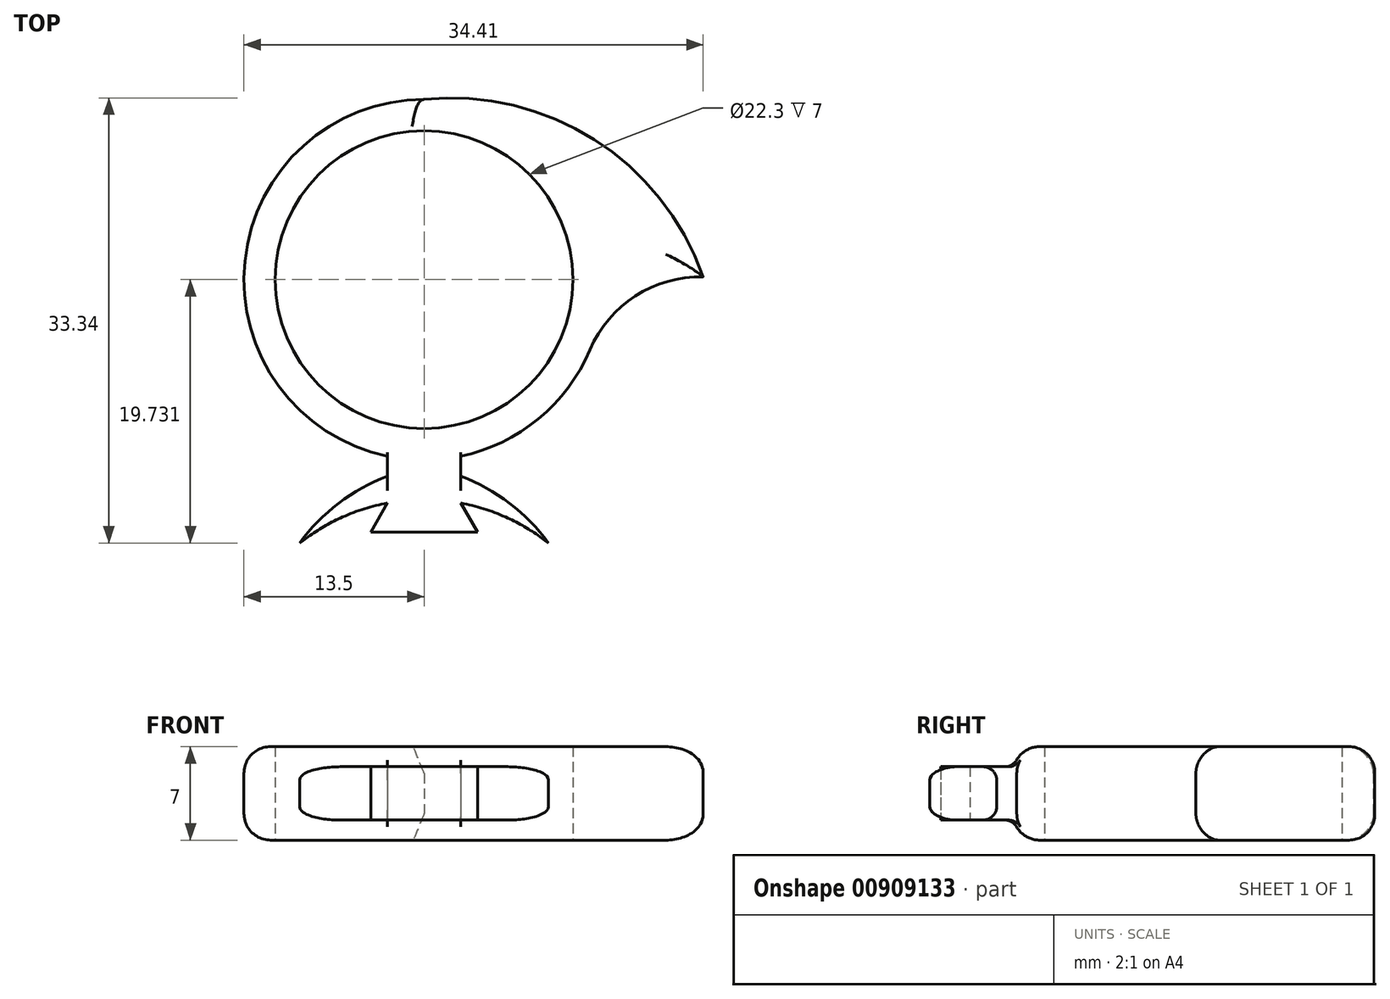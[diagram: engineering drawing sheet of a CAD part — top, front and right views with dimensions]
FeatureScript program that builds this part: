
annotation { "Feature Type Name" : "Feature", "Feature Type Description" : "" }
export const myFeature = defineFeature(function(context is Context, id is Id, definition is map)
    precondition{}
    {
        {
            var Q0;
            Q0=qCreatedBy(makeId("Top.planeOp"),FACE);
            var sketch = newSketch(context, id + "F0", { "sketchPlane" : qUnion([Q0])});
            skLineSegment(sketch, "E0", {"start": v(0, 0) * mm, "end": v(-4, 0) * mm});
            skLineSegment(sketch, "E1", {"start": v(-4, 0) * mm, "end": v(-2.75, 2.17) * mm});
            skLineSegment(sketch, "E2.MirrorCS", {"start": v(4, 0) * mm, "end": v(2.75, 2.17) * mm});
            skLineSegment(sketch, "E3.MirrorCS", {"start": v(0, 0) * mm, "end": v(4, 0) * mm});
            skPoint(sketch, "E4", {"position": v(0, 2.42) * mm});
            skCircle(sketch, "E5", {"center": v(0, 18.9) * mm, "radius": 11.15 * mm});
            skLineSegment(sketch, "E6", {"start": v(-2.75, 4.18) * mm, "end": v(-2.75, 5.68) * mm});
            skLineSegment(sketch, "E7", {"start": v(2.75, 4.18) * mm, "end": v(2.75, 5.68) * mm});
            skArc(sketch, "E8", {"start": v(20.91, 19.1) * mm, "mid": v(15.83, 17.67) * mm, "end": v(12.43, 13.64) * mm});
            skArc(sketch, "E9", {"start": v(20.91, 19.1) * mm, "mid": v(12.76, 29.38) * mm, "end": v(0, 32.4) * mm});
            skPoint(sketch, "E10", {"position": v(-9.32, -0.83) * mm});
            skPoint(sketch, "E11.MirrorP", {"position": v(9.32, -0.83) * mm});
            skArc(sketch, "E12", {"start": v(-2.75, 4.18) * mm, "mid": v(-6.4, 2.16) * mm, "end": v(-9.32, -0.83) * mm});
            skArc(sketch, "E13.MirrorCS", {"start": v(2.75, 4.18) * mm, "mid": v(6.4, 2.16) * mm, "end": v(9.32, -0.83) * mm});
            skArc(sketch, "E14", {"start": v(-2.75, 2.17) * mm, "mid": v(-6.22, 1.07) * mm, "end": v(-9.32, -0.83) * mm});
            skArc(sketch, "E15.MirrorCS", {"start": v(2.75, 2.17) * mm, "mid": v(6.22, 1.07) * mm, "end": v(9.32, -0.83) * mm});
            skArc(sketch, "E16", {"start": v(2.75, 2.17) * mm, "mid": v(0, 2.42) * mm, "end": v(-2.75, 2.17) * mm});
            skCircle(sketch, "E17", {"center": v(0, 18.9) * mm, "radius": 13.5 * mm});
            skSolve(sketch);
        }
        {
            var Q0;
            Q0=makeQuery(id+"F0.imprint","IMPRINT",FACE,{"disambiguationData":[TD([[makeQuery(id+"F0.imprint","IMPRINT",EDGE,{"derivedFrom":sQuery(id+"F0.wireOp",EDGE,"E5")}),-1.0]])]});
            var Q1;
            {var subQ0=sQuery(id+"F0.wireOp",EDGE,"E8");Q1=makeQuery(id+"F0.imprint","IMPRINT",FACE,{"disambiguationData":[TD([[makeQuery(id+"F0.imprint","IMPRINT",EDGE,{"derivedFrom":subQ0}),-1.0]])]});}
            extrude(context, id + "F1", {"entities" : qUnion([Q0, Q1]), "endBound" : BoundingType.SYMMETRIC, "depth" : 7 * mm, "offsetDistance" : 25 * mm});
        }
        {
            var Q0;
            {var subQ1=sQuery(id+"F0.wireOp",EDGE,"E6");Q0=makeQuery(id+"F0.imprint","IMPRINT",FACE,{"disambiguationData":[TD([[makeQuery(id+"F0.imprint","IMPRINT",EDGE,{"derivedFrom":subQ1}),-1.0]])]});}
            var Q1;
            Q1=makeQuery(id+"F0.imprint","IMPRINT",FACE,{"disambiguationData":[TD([[makeQuery(id+"F0.imprint","IMPRINT",EDGE,{"derivedFrom":sQuery(id+"F0.wireOp",EDGE,"E0")}),-1.0]])]});
            extrude(context, id + "F2", {"entities" : qUnion([Q0, Q1]), "operationType" : NewBodyOperationType.ADD, "endBound" : BoundingType.SYMMETRIC, "depth" : 4 * mm, "offsetDistance" : 25 * mm});
        }
        {
            var Q0;
            Q0=makeQuery(id+"F0.imprint","IMPRINT",FACE,{"disambiguationData":[TD([[makeQuery(id+"F0.imprint","IMPRINT",EDGE,{"derivedFrom":sQuery(id+"F0.wireOp",EDGE,"E0")}),-1.0]])]});
            extrude(context, id + "F3", {"entities" : qUnion([Q0]), "operationType" : NewBodyOperationType.ADD, "endBound" : BoundingType.SYMMETRIC, "depth" : 4 * mm, "offsetDistance" : 25 * mm});
        }
        {
            var Q0;
            Q0=makeQuery(id+"F1.opExtrude","CAP_EDGE",EDGE,{"disambiguationData":[OSD([sQuery(id+"F0.wireOp",EDGE,"E9")])],"isStart":true});
            var Q1;
            Q1=makeQuery(id+"F1.opExtrude","CAP_EDGE",EDGE,{"disambiguationData":[OSD([sQuery(id+"F0.wireOp",EDGE,"E9")])],"isStart":false});
            var Q2;
            {var subQ0=sQuery(id+"F0.wireOp",EDGE,"E9");var subQ2=sQuery(id+"F0.wireOp",EDGE,"L7pMj4X7-lkaH-sN8L-0iu3-v5NUff6WiaXn");Q2=makeQuery(id+"F2.boolean.opBoolean","SPLIT",EDGE,{"disambiguationData":[TD([makeQuery(id+"F1.opExtrude","SWEPT_FACE",FACE,{"disambiguationData":[OSD([subQ0])]})])],"derivedFrom":makeQuery(id+"F1.opExtrude","CAP_EDGE",EDGE,{"disambiguationData":[OSD([subQ2])],"isStart":false})});}
            var Q3;
            {var subQ1=sQuery(id+"F0.wireOp",EDGE,"L7pMj4X7-lkaH-sN8L-0iu3-v5NUff6WiaXn");var subQ2=sQuery(id+"F0.wireOp",EDGE,"E9");Q3=makeQuery(id+"F2.boolean.opBoolean","SPLIT",EDGE,{"disambiguationData":[TD([makeQuery(id+"F1.opExtrude","SWEPT_FACE",FACE,{"disambiguationData":[OSD([subQ2])]})])],"derivedFrom":makeQuery(id+"F1.opExtrude","CAP_EDGE",EDGE,{"disambiguationData":[OSD([subQ1])],"isStart":true})});}
            var Q4;
            Q4=makeQuery(id+"F1.opExtrude","CAP_EDGE",EDGE,{"disambiguationData":[OSD([sQuery(id+"F0.wireOp",EDGE,"E8")])],"isStart":true});
            var Q5;
            Q5=makeQuery(id+"F1.opExtrude","CAP_EDGE",EDGE,{"disambiguationData":[OSD([sQuery(id+"F0.wireOp",EDGE,"E8")])],"isStart":false});
            var Q6;
            {var subQ0=sQuery(id+"F0.wireOp",EDGE,"E8");var subQ2=sQuery(id+"F0.wireOp",EDGE,"L7pMj4X7-lkaH-sN8L-0iu3-v5NUff6WiaXn");Q6=makeQuery(id+"F2.boolean.opBoolean","SPLIT",EDGE,{"disambiguationData":[TD([makeQuery(id+"F1.opExtrude","SWEPT_FACE",FACE,{"disambiguationData":[OSD([subQ0])]})])],"derivedFrom":makeQuery(id+"F1.opExtrude","CAP_EDGE",EDGE,{"disambiguationData":[OSD([subQ2])],"isStart":false})});}
            var Q7;
            {var subQ1=sQuery(id+"F0.wireOp",EDGE,"L7pMj4X7-lkaH-sN8L-0iu3-v5NUff6WiaXn");var subQ2=sQuery(id+"F0.wireOp",EDGE,"E8");Q7=makeQuery(id+"F2.boolean.opBoolean","SPLIT",EDGE,{"disambiguationData":[TD([makeQuery(id+"F1.opExtrude","SWEPT_FACE",FACE,{"disambiguationData":[OSD([subQ2])]})])],"derivedFrom":makeQuery(id+"F1.opExtrude","CAP_EDGE",EDGE,{"disambiguationData":[OSD([subQ1])],"isStart":true})});}
            fillet(context, id + "F4", {"entities" : qUnion([Q0, Q1, Q2, Q3, Q4, Q5, Q6, Q7]), "radius" : 1.9 * mm, "allowEdgeOverflow" : false});
        }
        {
            var Q0;
            {var subQ0=sQuery(id+"F0.wireOp",EDGE,"ZRtLBS3C-WQQk-BILs-9W3d-OrrpI6sGSa5z");var subQ1=sQuery(id+"F0.wireOp",EDGE,"L7pMj4X7-lkaH-sN8L-0iu3-v5NUff6WiaXn");Q0=makeQuery(id+"F4.opFillet","BLEND_EDGE",EDGE,{"blendedFrom":[makeQuery(id+"F1.opExtrude","CAP_EDGE",EDGE,{"disambiguationData":[OSD([subQ1])],"isStart":true}),makeQuery(id+"F3.boolean.opBoolean","MERGE",FACE,{"derivedFrom":[makeQuery(id+"F2.opExtrude","CAP_FACE",FACE,{"disambiguationData":[OSD([subQ1,sQuery(id+"F0.wireOp",EDGE,"yEclmRM6-fmEu-YwPp-0boo-BpuIT0I3fzAk"),sQuery(id+"F0.wireOp",EDGE,"8e367950-b865-4a29-9308-db6c61288a710.MirrorCS"),sQuery(id+"F0.wireOp",EDGE,"yja5ZLDi-WZ6y-1e2p-gRGM-Dr0lzgQqEL6q"),sQuery(id+"F0.wireOp",EDGE,"729beffa-f1f2-4303-a60b-b9acdf640f0f0.MirrorCS"),sQuery(id+"F0.wireOp",EDGE,"E6"),sQuery(id+"F0.wireOp",EDGE,"E7"),subQ0])],"isStart":true}),makeQuery(id+"F3.opExtrude","CAP_FACE",FACE,{"disambiguationData":[OSD([sQuery(id+"F0.wireOp",EDGE,"E0"),sQuery(id+"F0.wireOp",EDGE,"E1"),sQuery(id+"F0.wireOp",EDGE,"E2.MirrorCS"),sQuery(id+"F0.wireOp",EDGE,"E3.MirrorCS"),subQ0])],"isStart":true})]})],"blendedInto":[makeQuery(id+"F3.boolean.opBoolean","MERGE",FACE,{"derivedFrom":[makeQuery(id+"F2.opExtrude","CAP_FACE",FACE,{"disambiguationData":[OSD([subQ1,sQuery(id+"F0.wireOp",EDGE,"yEclmRM6-fmEu-YwPp-0boo-BpuIT0I3fzAk"),sQuery(id+"F0.wireOp",EDGE,"8e367950-b865-4a29-9308-db6c61288a710.MirrorCS"),sQuery(id+"F0.wireOp",EDGE,"yja5ZLDi-WZ6y-1e2p-gRGM-Dr0lzgQqEL6q"),sQuery(id+"F0.wireOp",EDGE,"729beffa-f1f2-4303-a60b-b9acdf640f0f0.MirrorCS"),sQuery(id+"F0.wireOp",EDGE,"E6"),sQuery(id+"F0.wireOp",EDGE,"E7"),subQ0])],"isStart":true}),makeQuery(id+"F3.opExtrude","CAP_FACE",FACE,{"disambiguationData":[OSD([sQuery(id+"F0.wireOp",EDGE,"E0"),sQuery(id+"F0.wireOp",EDGE,"E1"),sQuery(id+"F0.wireOp",EDGE,"E2.MirrorCS"),sQuery(id+"F0.wireOp",EDGE,"E3.MirrorCS"),subQ0])],"isStart":true})]})]});}
            var Q1;
            {var subQ0=sQuery(id+"F0.wireOp",EDGE,"ZRtLBS3C-WQQk-BILs-9W3d-OrrpI6sGSa5z");var subQ1=sQuery(id+"F0.wireOp",EDGE,"L7pMj4X7-lkaH-sN8L-0iu3-v5NUff6WiaXn");Q1=makeQuery(id+"F4.opFillet","BLEND_EDGE",EDGE,{"blendedFrom":[makeQuery(id+"F1.opExtrude","CAP_EDGE",EDGE,{"disambiguationData":[OSD([subQ1])],"isStart":false}),makeQuery(id+"F3.boolean.opBoolean","MERGE",FACE,{"derivedFrom":[makeQuery(id+"F2.opExtrude","CAP_FACE",FACE,{"disambiguationData":[OSD([subQ1,sQuery(id+"F0.wireOp",EDGE,"yEclmRM6-fmEu-YwPp-0boo-BpuIT0I3fzAk"),sQuery(id+"F0.wireOp",EDGE,"8e367950-b865-4a29-9308-db6c61288a710.MirrorCS"),sQuery(id+"F0.wireOp",EDGE,"yja5ZLDi-WZ6y-1e2p-gRGM-Dr0lzgQqEL6q"),sQuery(id+"F0.wireOp",EDGE,"729beffa-f1f2-4303-a60b-b9acdf640f0f0.MirrorCS"),sQuery(id+"F0.wireOp",EDGE,"E6"),sQuery(id+"F0.wireOp",EDGE,"E7"),subQ0])],"isStart":false}),makeQuery(id+"F3.opExtrude","CAP_FACE",FACE,{"disambiguationData":[OSD([sQuery(id+"F0.wireOp",EDGE,"E0"),sQuery(id+"F0.wireOp",EDGE,"E1"),sQuery(id+"F0.wireOp",EDGE,"E2.MirrorCS"),sQuery(id+"F0.wireOp",EDGE,"E3.MirrorCS"),subQ0])],"isStart":false})]})],"blendedInto":[makeQuery(id+"F3.boolean.opBoolean","MERGE",FACE,{"derivedFrom":[makeQuery(id+"F2.opExtrude","CAP_FACE",FACE,{"disambiguationData":[OSD([subQ1,sQuery(id+"F0.wireOp",EDGE,"yEclmRM6-fmEu-YwPp-0boo-BpuIT0I3fzAk"),sQuery(id+"F0.wireOp",EDGE,"8e367950-b865-4a29-9308-db6c61288a710.MirrorCS"),sQuery(id+"F0.wireOp",EDGE,"yja5ZLDi-WZ6y-1e2p-gRGM-Dr0lzgQqEL6q"),sQuery(id+"F0.wireOp",EDGE,"729beffa-f1f2-4303-a60b-b9acdf640f0f0.MirrorCS"),sQuery(id+"F0.wireOp",EDGE,"E6"),sQuery(id+"F0.wireOp",EDGE,"E7"),subQ0])],"isStart":false}),makeQuery(id+"F3.opExtrude","CAP_FACE",FACE,{"disambiguationData":[OSD([sQuery(id+"F0.wireOp",EDGE,"E0"),sQuery(id+"F0.wireOp",EDGE,"E1"),sQuery(id+"F0.wireOp",EDGE,"E2.MirrorCS"),sQuery(id+"F0.wireOp",EDGE,"E3.MirrorCS"),subQ0])],"isStart":false})]})]});}
            var Q2;
            Q2=makeQuery(id+"F1.opExtrude","CAP_EDGE",EDGE,{"disambiguationData":[OSD([sQuery(id+"F0.wireOp",EDGE,"E17")])],"isStart":true});
            var Q3;
            Q3=makeQuery(id+"F1.opExtrude","CAP_EDGE",EDGE,{"disambiguationData":[OSD([sQuery(id+"F0.wireOp",EDGE,"E17")])],"isStart":false});
            fillet(context, id + "F5", {"entities" : qUnion([Q0, Q1, Q2, Q3]), "radius" : 2 * mm, "tangentPropagation" : true, "allowEdgeOverflow" : false});
        }
        {
            var Q0;
            {var subQ0=sQuery(id+"F0.wireOp",EDGE,"E17");Q0=makeQuery(id+"F5.opFillet","BLEND_EDGE",EDGE,{"blendedFrom":[makeQuery(id+"F1.opExtrude","CAP_EDGE",EDGE,{"disambiguationData":[OSD([subQ0])],"isStart":false}),makeQuery(id+"F2.opExtrude","CAP_FACE",FACE,{"disambiguationData":[OSD([sQuery(id+"F0.wireOp",EDGE,"E0"),sQuery(id+"F0.wireOp",EDGE,"E1"),sQuery(id+"F0.wireOp",EDGE,"E2.MirrorCS"),sQuery(id+"F0.wireOp",EDGE,"E3.MirrorCS"),sQuery(id+"F0.wireOp",EDGE,"E6"),sQuery(id+"F0.wireOp",EDGE,"E7"),sQuery(id+"F0.wireOp",EDGE,"E12"),sQuery(id+"F0.wireOp",EDGE,"E13.MirrorCS"),sQuery(id+"F0.wireOp",EDGE,"E14"),sQuery(id+"F0.wireOp",EDGE,"E15.MirrorCS"),subQ0])],"isStart":false})],"blendedInto":[makeQuery(id+"F2.opExtrude","CAP_FACE",FACE,{"disambiguationData":[OSD([sQuery(id+"F0.wireOp",EDGE,"E0"),sQuery(id+"F0.wireOp",EDGE,"E1"),sQuery(id+"F0.wireOp",EDGE,"E2.MirrorCS"),sQuery(id+"F0.wireOp",EDGE,"E3.MirrorCS"),sQuery(id+"F0.wireOp",EDGE,"E6"),sQuery(id+"F0.wireOp",EDGE,"E7"),sQuery(id+"F0.wireOp",EDGE,"E12"),sQuery(id+"F0.wireOp",EDGE,"E13.MirrorCS"),sQuery(id+"F0.wireOp",EDGE,"E14"),sQuery(id+"F0.wireOp",EDGE,"E15.MirrorCS"),subQ0])],"isStart":false})]});}
            var Q1;
            {var subQ0=sQuery(id+"F0.wireOp",EDGE,"E17");Q1=makeQuery(id+"F5.opFillet","BLEND_EDGE",EDGE,{"blendedFrom":[makeQuery(id+"F1.opExtrude","CAP_EDGE",EDGE,{"disambiguationData":[OSD([subQ0])],"isStart":true}),makeQuery(id+"F2.opExtrude","CAP_FACE",FACE,{"disambiguationData":[OSD([sQuery(id+"F0.wireOp",EDGE,"E0"),sQuery(id+"F0.wireOp",EDGE,"E1"),sQuery(id+"F0.wireOp",EDGE,"E2.MirrorCS"),sQuery(id+"F0.wireOp",EDGE,"E3.MirrorCS"),sQuery(id+"F0.wireOp",EDGE,"E6"),sQuery(id+"F0.wireOp",EDGE,"E7"),sQuery(id+"F0.wireOp",EDGE,"E12"),sQuery(id+"F0.wireOp",EDGE,"E13.MirrorCS"),sQuery(id+"F0.wireOp",EDGE,"E14"),sQuery(id+"F0.wireOp",EDGE,"E15.MirrorCS"),subQ0])],"isStart":true})],"blendedInto":[makeQuery(id+"F2.opExtrude","CAP_FACE",FACE,{"disambiguationData":[OSD([sQuery(id+"F0.wireOp",EDGE,"E0"),sQuery(id+"F0.wireOp",EDGE,"E1"),sQuery(id+"F0.wireOp",EDGE,"E2.MirrorCS"),sQuery(id+"F0.wireOp",EDGE,"E3.MirrorCS"),sQuery(id+"F0.wireOp",EDGE,"E6"),sQuery(id+"F0.wireOp",EDGE,"E7"),sQuery(id+"F0.wireOp",EDGE,"E12"),sQuery(id+"F0.wireOp",EDGE,"E13.MirrorCS"),sQuery(id+"F0.wireOp",EDGE,"E14"),sQuery(id+"F0.wireOp",EDGE,"E15.MirrorCS"),subQ0])],"isStart":true})]});}
            var Q2;
            Q2=makeQuery(id+"F2.opExtrude","CAP_EDGE",EDGE,{"disambiguationData":[OSD([sQuery(id+"F0.wireOp",EDGE,"E12")])],"isStart":false});
            var Q3;
            Q3=makeQuery(id+"F2.opExtrude","CAP_EDGE",EDGE,{"disambiguationData":[OSD([sQuery(id+"F0.wireOp",EDGE,"E12")])],"isStart":true});
            var Q4;
            Q4=makeQuery(id+"F2.opExtrude","CAP_EDGE",EDGE,{"disambiguationData":[OSD([sQuery(id+"F0.wireOp",EDGE,"E13.MirrorCS")])],"isStart":false});
            var Q5;
            Q5=makeQuery(id+"F2.opExtrude","CAP_EDGE",EDGE,{"disambiguationData":[OSD([sQuery(id+"F0.wireOp",EDGE,"E13.MirrorCS")])],"isStart":true});
            fillet(context, id + "F6", {"entities" : qUnion([Q0, Q1, Q2, Q3, Q4, Q5]), "radius" : 1 * mm, "tangentPropagation" : true, "allowEdgeOverflow" : false});
        }
    });
